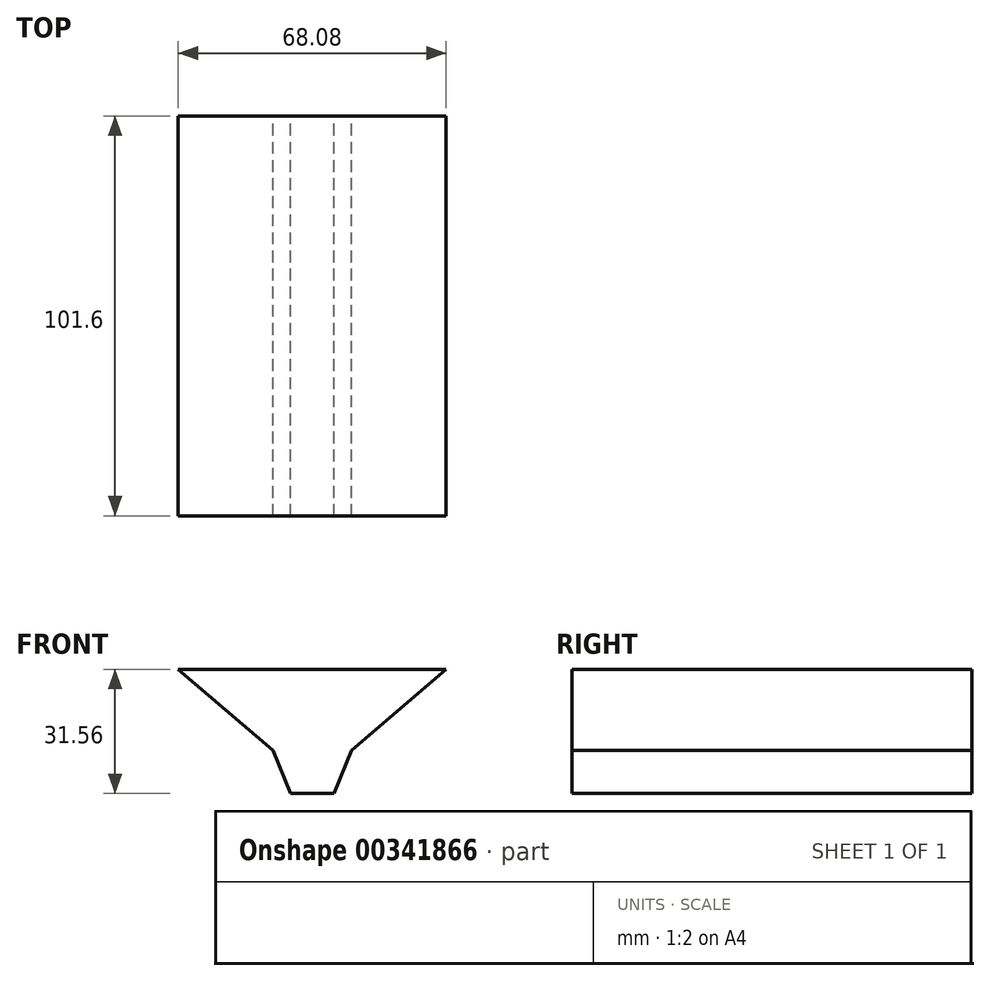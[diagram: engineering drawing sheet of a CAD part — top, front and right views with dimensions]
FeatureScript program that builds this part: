
annotation { "Feature Type Name" : "Feature", "Feature Type Description" : "" }
export const myFeature = defineFeature(function(context is Context, id is Id, definition is map)
    precondition{}
    {
        {
            var Q0;
            Q0=qCreatedBy(makeId("Front.planeOp"),FACE);
            var sketch = newSketch(context, id + "F0", { "sketchPlane" : qUnion([Q0])});
            skLineSegment(sketch, "E0", {"start": v(-9.91, 0) * mm, "end": v(-33.97, 20.56) * mm});
            skLineSegment(sketch, "E1", {"start": v(-33.97, 20.56) * mm, "end": v(34.11, 20.56) * mm});
            skLineSegment(sketch, "E2", {"start": v(34.11, 20.56) * mm, "end": v(10.05, 0) * mm});
            skLineSegment(sketch, "E3", {"start": v(10.05, 0) * mm, "end": v(5.6, -11) * mm});
            skLineSegment(sketch, "E4", {"start": v(5.6, -11) * mm, "end": v(-5.46, -11) * mm});
            skLineSegment(sketch, "E5", {"start": v(-5.46, -11) * mm, "end": v(-9.91, 0) * mm});
            skLineSegment(sketch, "E6", {"start": v(0.07, 20.56) * mm, "end": v(0.07, -11) * mm});
            skSolve(sketch);
        }
        {
            var Q0;
            Q0 = qSketchRegion(id + "F0", true);
            extrude(context, id + "F1", {"entities" : qUnion([Q0]), "depth" : 101.6 * mm});
        }
    });
